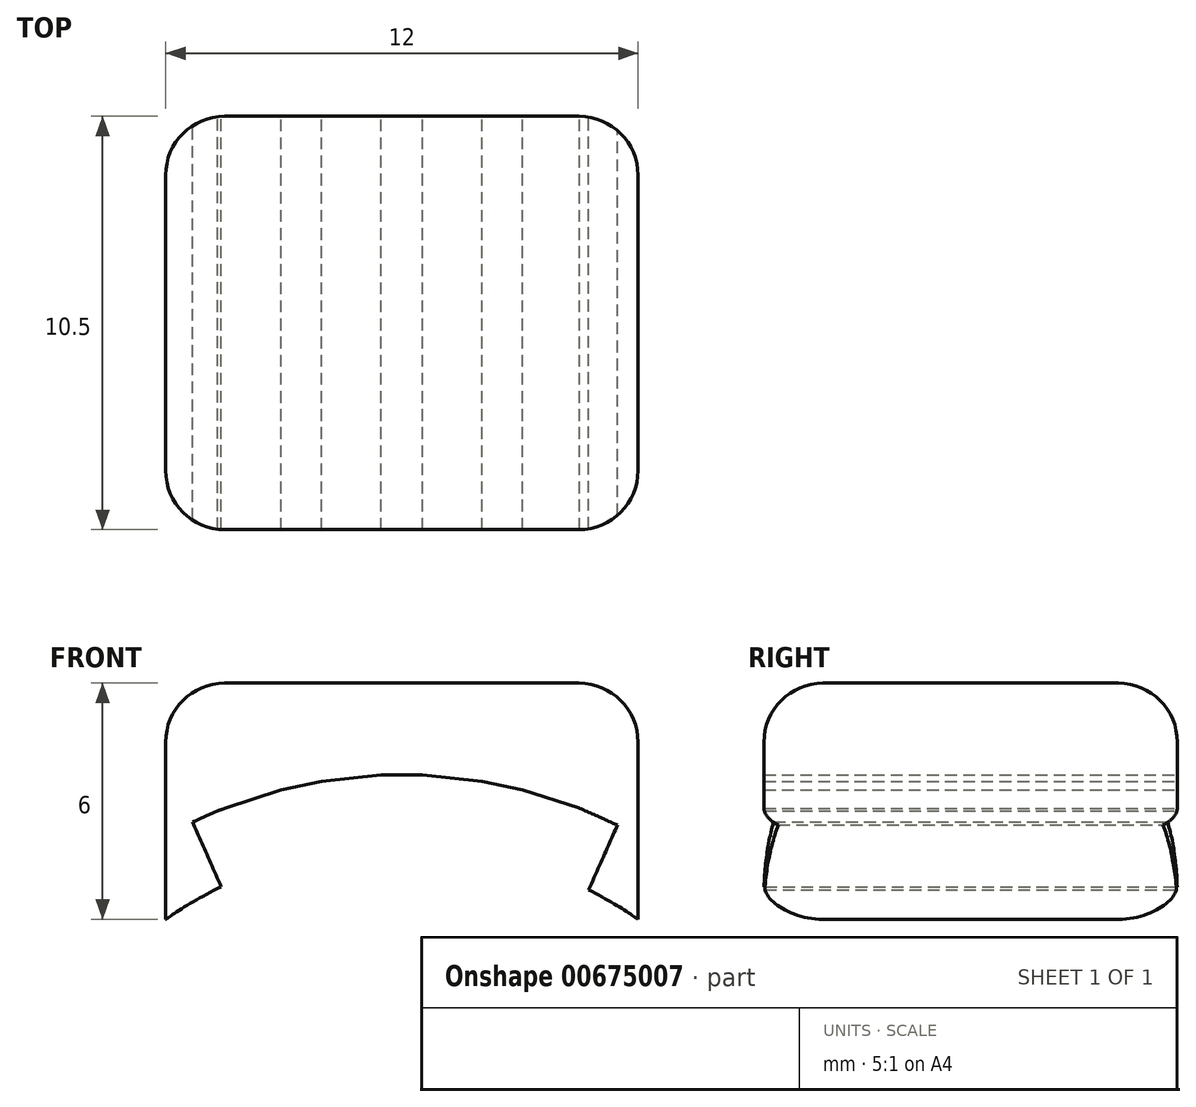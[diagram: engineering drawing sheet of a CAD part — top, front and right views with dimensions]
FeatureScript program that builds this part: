
annotation { "Feature Type Name" : "Feature", "Feature Type Description" : "" }
export const myFeature = defineFeature(function(context is Context, id is Id, definition is map)
    precondition{}
    {
        {
            assignVariable(context, id + "F0", {"name" : "Faktor", "anyValue" : 1.5});
        }
        {
            var Q0;
            Q0=qCreatedBy(makeId("Front.planeOp"),FACE);
            var sketch = newSketch(context, id + "F1", { "sketchPlane" : qUnion([Q0])});
            skArc(sketch, "E0", {"start": v(6, 8.62) * mm, "mid": v(5.39, 9.01) * mm, "end": v(4.75, 9.37) * mm});
            skLineSegment(sketch, "E1.bottom", {"start": v(-6, 14.62) * mm, "end": v(6, 14.62) * mm});
            skLineSegment(sketch, "E1.left", {"start": v(-6, 14.62) * mm, "end": v(-6, 8.62) * mm});
            skLineSegment(sketch, "E1.right", {"start": v(6, 14.62) * mm, "end": v(6, 8.62) * mm});
            skLineSegment(sketch, "E2.top", {"start": v(-0.53, 12.29) * mm, "end": v(0.53, 12.29) * mm});
            skLineSegment(sketch, "E2.left", {"start": v(-0.53, 10.49) * mm, "end": v(-0.53, 12.29) * mm, "construction": true});
            skLineSegment(sketch, "E2.right", {"start": v(0.53, 10.49) * mm, "end": v(0.53, 12.29) * mm, "construction": true});
            skArc(sketch, "E3.trimOffspring", {"start": v(-0.53, 10.49) * mm, "mid": v(-1.1, 10.44) * mm, "end": v(-1.67, 10.37) * mm, "construction": true});
            skLineSegment(sketch, "E4", {"start": v(0, 0) * mm, "end": v(-2.93, 13.8) * mm, "construction": true});
            skLineSegment(sketch, "E5", {"start": v(0, 0) * mm, "end": v(2.92, 13.72) * mm, "construction": true});
            skLineSegment(sketch, "E6", {"start": v(-2.7, 10.15) * mm, "end": v(-3.07, 11.9) * mm, "construction": true});
            skLineSegment(sketch, "E7", {"start": v(-3.07, 11.9) * mm, "end": v(-2.04, 12.13) * mm});
            skLineSegment(sketch, "E8", {"start": v(-2.04, 12.13) * mm, "end": v(-1.67, 10.37) * mm, "construction": true});
            skArc(sketch, "E9.trimOffspring", {"start": v(-2.7, 10.15) * mm, "mid": v(-3.33, 9.96) * mm, "end": v(-3.95, 9.73) * mm, "construction": true});
            skLineSegment(sketch, "E10", {"start": v(1.67, 10.37) * mm, "end": v(2.04, 12.13) * mm, "construction": true});
            skLineSegment(sketch, "E11", {"start": v(2.04, 12.13) * mm, "end": v(3.07, 11.9) * mm});
            skLineSegment(sketch, "E12", {"start": v(3.07, 11.9) * mm, "end": v(2.7, 10.15) * mm, "construction": true});
            skArc(sketch, "E13.trimOffspring", {"start": v(1.67, 10.37) * mm, "mid": v(1.1, 10.44) * mm, "end": v(0.53, 10.49) * mm, "construction": true});
            skLineSegment(sketch, "E14", {"start": v(0, 0) * mm, "end": v(5.8, 13) * mm, "construction": true});
            skLineSegment(sketch, "E15", {"start": v(0, 0) * mm, "end": v(-5.84, 13.12) * mm, "construction": true});
            skLineSegment(sketch, "E16", {"start": v(-4.59, 9.44) * mm, "end": v(-5.32, 11.09) * mm});
            skLineSegment(sketch, "E17", {"start": v(-5.32, 11.09) * mm, "end": v(-4.68, 11.37) * mm});
            skLineSegment(sketch, "E18", {"start": v(-4.68, 11.37) * mm, "end": v(-3.95, 9.73) * mm, "construction": true});
            skArc(sketch, "E19.trimOffspring", {"start": v(-4.59, 9.44) * mm, "mid": v(-5.31, 9.06) * mm, "end": v(-6, 8.62) * mm});
            skLineSegment(sketch, "E20", {"start": v(3.79, 9.8) * mm, "end": v(4.52, 11.44) * mm, "construction": true});
            skLineSegment(sketch, "E21", {"start": v(4.52, 11.44) * mm, "end": v(5.48, 11.01) * mm});
            skLineSegment(sketch, "E22", {"start": v(5.48, 11.01) * mm, "end": v(4.75, 9.37) * mm});
            skArc(sketch, "E23.trimOffspring", {"start": v(3.79, 9.8) * mm, "mid": v(3.24, 9.99) * mm, "end": v(2.7, 10.15) * mm, "construction": true});
            skLineSegment(sketch, "E24", {"start": v(-4.68, 11.37) * mm, "end": v(-3.07, 11.9) * mm});
            skLineSegment(sketch, "E25", {"start": v(-2.04, 12.13) * mm, "end": v(-0.53, 12.29) * mm});
            skLineSegment(sketch, "E26", {"start": v(0.53, 12.29) * mm, "end": v(2.04, 12.13) * mm});
            skLineSegment(sketch, "E27", {"start": v(3.07, 11.9) * mm, "end": v(4.52, 11.44) * mm});
            skSolve(sketch);
        }
        {
            var Q0;
            Q0=qSketchRegion(id+"F1",true);
            extrude(context, id + "F2", {"entities" : qUnion([Q0]), "depth" : getVariable(context, 'Faktor') * 7 * mm, "offsetDistance" : 25 * mm});
        }
        {
            var Q0;
            Q0=makeQuery(id+"F2.opExtrude","CAP_EDGE",EDGE,{"disambiguationData":[OSD([sQuery(id+"F1.wireOp",EDGE,"E1.left")])],"isStart":false});
            var Q1;
            Q1=makeQuery(id+"F2.opExtrude","CAP_EDGE",EDGE,{"disambiguationData":[OSD([sQuery(id+"F1.wireOp",EDGE,"E1.right")])],"isStart":false});
            var Q2;
            Q2=makeQuery(id+"F2.opExtrude","CAP_EDGE",EDGE,{"disambiguationData":[OSD([sQuery(id+"F1.wireOp",EDGE,"E1.right")])],"isStart":true});
            var Q3;
            Q3=makeQuery(id+"F2.opExtrude","CAP_EDGE",EDGE,{"disambiguationData":[OSD([sQuery(id+"F1.wireOp",EDGE,"E1.left")])],"isStart":true});
            var Q4;
            Q4=makeQuery(id+"F2.opExtrude","SWEPT_FACE",FACE,{"disambiguationData":[OSD([sQuery(id+"F1.wireOp",EDGE,"E1.bottom")])]});
            fillet(context, id + "F3", {"entities" : qUnion([Q0, Q1, Q2, Q3, Q4]), "radius" : getVariable(context, 'Faktor') * 1 * mm, "tangentPropagation" : true, "allowEdgeOverflow" : false});
        }
    });
